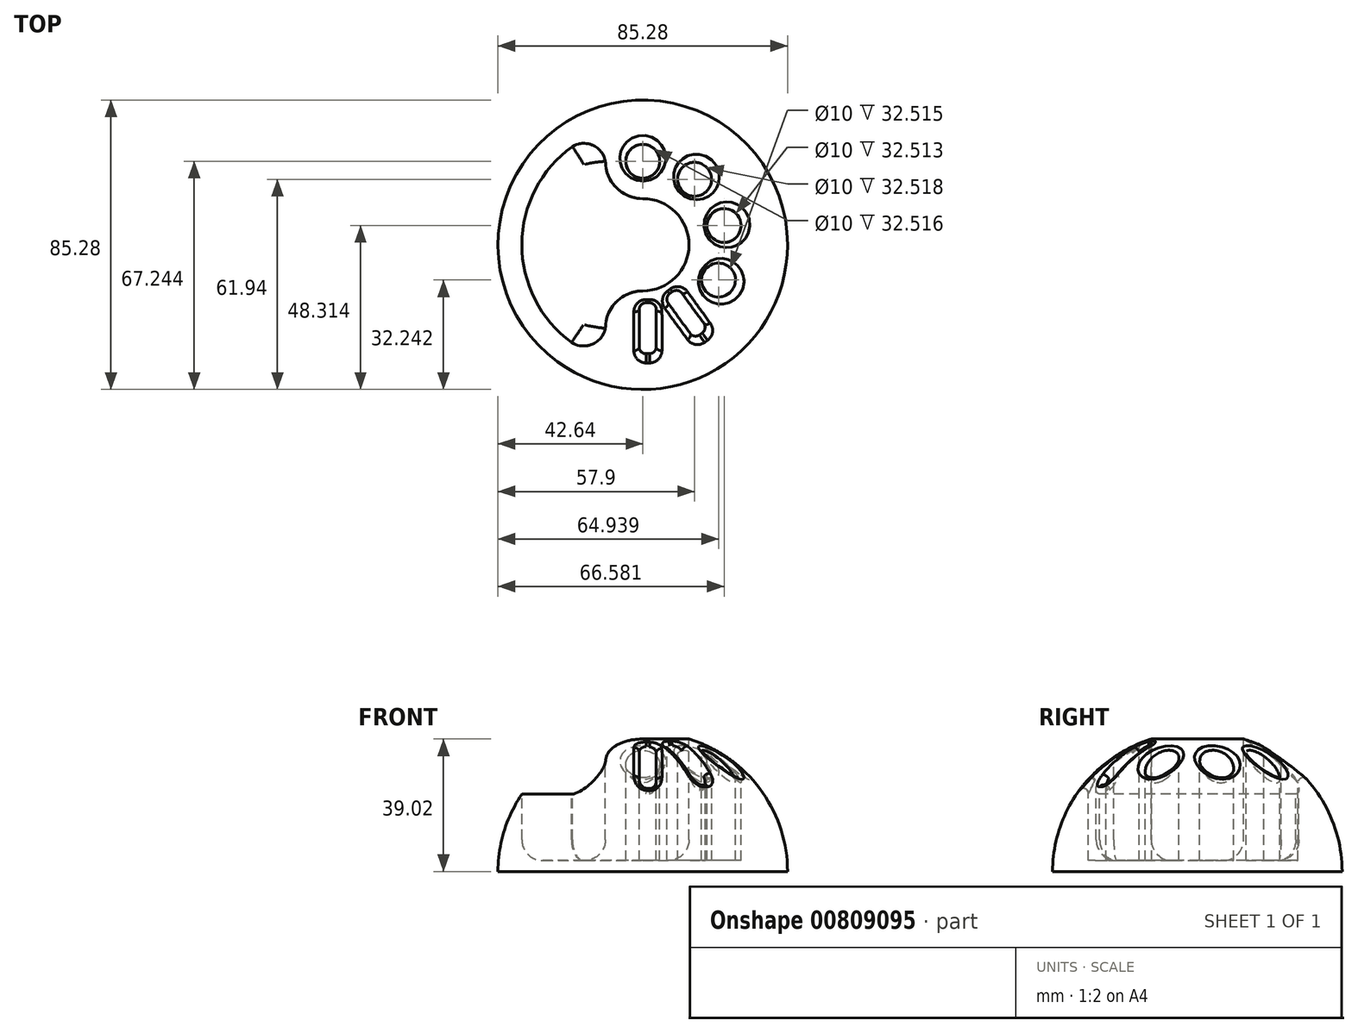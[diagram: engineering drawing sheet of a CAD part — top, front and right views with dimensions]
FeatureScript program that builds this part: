
annotation { "Feature Type Name" : "Feature", "Feature Type Description" : "" }
export const myFeature = defineFeature(function(context is Context, id is Id, definition is map)
    precondition{}
    {
        {
            var Q0;
            Q0=qCreatedBy(makeId("Top.planeOp"),FACE);
            var sketch = newSketch(context, id + "F0", { "sketchPlane" : qUnion([Q0])});
            skPoint(sketch, "E0.middle", {"position": v(0, 0) * mm});
            skCircle(sketch, "E1", {"center": v(0, 0) * mm, "radius": 42.64 * mm});
            skPoint(sketch, "E0.left.end.orphan", {"position": v(-44.45, 44.45) * mm});
            skPoint(sketch, "E0.bottom.start.orphan", {"position": v(-44.45, -44.45) * mm});
            skPoint(sketch, "E0.right.end.orphan", {"position": v(44.45, 44.45) * mm});
            skPoint(sketch, "E0.right.start.orphan", {"position": v(44.45, -44.45) * mm});
            skSolve(sketch);
        }
        {
            var Q0;
            Q0=makeQuery(id+"F0.imprint","IMPRINT",FACE,{"disambiguationData":[TD([[makeQuery(id+"F0.imprint","IMPRINT",EDGE,{"derivedFrom":sQuery(id+"F0.wireOp",EDGE,"E0.bottom")}),1.0]])]});
            var Q1;
            Q1=makeQuery(id+"F0.imprint","IMPRINT",FACE,{"disambiguationData":[TD([[makeQuery(id+"F0.imprint","IMPRINT",EDGE,{"derivedFrom":sQuery(id+"F0.wireOp",EDGE,"E1")}),1.0]])]});
            extrude(context, id + "F1", {"entities" : qUnion([Q0, Q1]), "depth" : 50.8 * mm, "offsetDistance" : 25.4 * mm, "hasSecondDirection" : true, "secondDirectionOppositeDirection" : false, "secondDirectionDepth" : 10 * mm});
        }
        {
            var Q0;
            Q0=makeQuery(id+"F1.opExtrude","CAP_FACE",FACE,{"disambiguationData":[OSD([sQuery(id+"F0.wireOp",EDGE,"E1")])],"isStart":false});
            var sketch = newSketch(context, id + "F2", { "sketchPlane" : qUnion([Q0])});
            skCircle(sketch, "E2", {"center": v(0, 24.6) * mm, "radius": 5 * mm});
            skCircle(sketch, "E3.1.0", {"center": v(15.26, 19.3) * mm, "radius": 5 * mm});
            skCircle(sketch, "E3.2.0", {"center": v(23.94, 5.67) * mm, "radius": 5 * mm});
            skCircle(sketch, "E3.3.0", {"center": v(22.3, -10.4) * mm, "radius": 5 * mm});
            skPoint(sketch, "E3.center", {"position": v(0, 0) * mm});
            skLineSegment(sketch, "E3.anchor1", {"start": v(0, 0) * mm, "end": v(0, 24.6) * mm, "construction": true});
            skLineSegment(sketch, "E3.anchor2", {"start": v(0, 0) * mm, "end": v(22.3, -10.4) * mm, "construction": true});
            skLineSegment(sketch, "E4.bottom", {"start": v(1.96, -32.1) * mm, "end": v(0.96, -32.1) * mm});
            skLineSegment(sketch, "E4.top", {"start": v(1.96, -17.1) * mm, "end": v(0.96, -17.1) * mm});
            skLineSegment(sketch, "E4.left", {"start": v(3.96, -30.1) * mm, "end": v(3.96, -19.1) * mm});
            skLineSegment(sketch, "E4.right", {"start": v(-1.04, -30.1) * mm, "end": v(-1.04, -19.1) * mm});
            skPoint(sketch, "E4.middle", {"position": v(1.46, -24.6) * mm});
            skPoint(sketch, "E5.visualSharp", {"position": v(-1.04, -17.1) * mm});
            skArc(sketch, "E5.filletArc", {"start": v(0.96, -17.1) * mm, "mid": v(-0.45, -17.68) * mm, "end": v(-1.04, -19.1) * mm});
            skPoint(sketch, "E6.visualSharp", {"position": v(3.96, -17.1) * mm});
            skArc(sketch, "E6.filletArc", {"start": v(3.96, -19.1) * mm, "mid": v(3.37, -17.68) * mm, "end": v(1.96, -17.1) * mm});
            skPoint(sketch, "E7.visualSharp", {"position": v(3.96, -32.1) * mm});
            skArc(sketch, "E7.filletArc", {"start": v(1.96, -32.1) * mm, "mid": v(3.37, -31.5) * mm, "end": v(3.96, -30.1) * mm});
            skPoint(sketch, "E8.visualSharp", {"position": v(-1.04, -32.1) * mm});
            skArc(sketch, "E8.filletArc", {"start": v(-1.04, -30.1) * mm, "mid": v(-0.45, -31.5) * mm, "end": v(0.96, -32.1) * mm});
            skPoint(sketch, "E9.1.0", {"position": v(10.33, -12.64) * mm});
            skLineSegment(sketch, "E9.1.1", {"start": v(17.98, -23.16) * mm, "end": v(11.5, -14.26) * mm});
            skArc(sketch, "E9.1.2", {"start": v(17.53, -25.95) * mm, "mid": v(18.33, -24.65) * mm, "end": v(17.98, -23.16) * mm});
            skArc(sketch, "E9.1.3", {"start": v(11.5, -14.26) * mm, "mid": v(10.2, -13.46) * mm, "end": v(8.72, -13.82) * mm});
            skLineSegment(sketch, "E9.1.4", {"start": v(8.72, -13.82) * mm, "end": v(7.9, -14.4) * mm});
            skArc(sketch, "E9.1.5", {"start": v(7.9, -14.4) * mm, "mid": v(7.1, -15.71) * mm, "end": v(7.46, -17.2) * mm});
            skLineSegment(sketch, "E9.1.6", {"start": v(13.93, -26.1) * mm, "end": v(7.46, -17.2) * mm});
            skArc(sketch, "E9.1.7", {"start": v(13.93, -26.1) * mm, "mid": v(15.24, -26.9) * mm, "end": v(16.72, -26.54) * mm});
            skLineSegment(sketch, "E9.1.8", {"start": v(17.53, -25.95) * mm, "end": v(16.72, -26.54) * mm});
            skPoint(sketch, "E9.center", {"position": v(0.3, -5.06) * mm});
            skLineSegment(sketch, "E9.anchor1", {"start": v(0.3, -5.06) * mm, "end": v(3.96, -19.1) * mm, "construction": true});
            skLineSegment(sketch, "E9.anchor2", {"start": v(0.3, -5.06) * mm, "end": v(11.5, -14.26) * mm, "construction": true});
            skArc(sketch, "E10", {"start": v(0, -13.6) * mm, "mid": v(13.6, 0) * mm, "end": v(0, 13.6) * mm});
            skArc(sketch, "E11", {"start": v(-11, 24.6) * mm, "mid": v(-7.78, 16.82) * mm, "end": v(0, 13.6) * mm});
            skArc(sketch, "E12", {"start": v(-20.72, 28.96) * mm, "mid": v(-35.6, 0.16) * mm, "end": v(-20.98, -28.77) * mm});
            skArc(sketch, "E13.1.0", {"start": v(0, -13.6) * mm, "mid": v(-7.78, -16.82) * mm, "end": v(-11, -24.6) * mm});
            skLineSegment(sketch, "E13.anchor2", {"start": v(0, 0) * mm, "end": v(0, -24.6) * mm, "construction": true});
            skArc(sketch, "E14", {"start": v(-11, 24.6) * mm, "mid": v(-15.28, 29.55) * mm, "end": v(-21.68, 28.25) * mm});
            skArc(sketch, "E15", {"start": v(-21.68, -28.25) * mm, "mid": v(-15.3, -29.48) * mm, "end": v(-11, -24.6) * mm});
            skSolve(sketch);
        }
        {
            var Q0;
            Q0=makeQuery(id+"F2.imprint","IMPRINT",FACE,{"disambiguationData":[TD([[makeQuery(id+"F2.imprint","IMPRINT",EDGE,{"derivedFrom":sQuery(id+"F2.wireOp",EDGE,"E10")}),1.0]])]});
            var Q1;
            Q1=makeQuery(id+"F2.imprint","IMPRINT",FACE,{"disambiguationData":[TD([[makeQuery(id+"F2.imprint","IMPRINT",EDGE,{"derivedFrom":sQuery(id+"F2.wireOp",EDGE,"E2")}),1.0]])]});
            var Q2;
            Q2=makeQuery(id+"F2.imprint","IMPRINT",FACE,{"disambiguationData":[TD([[makeQuery(id+"F2.imprint","IMPRINT",EDGE,{"derivedFrom":sQuery(id+"F2.wireOp",EDGE,"E3.1.0")}),1.0]])]});
            var Q3;
            Q3=makeQuery(id+"F2.imprint","IMPRINT",FACE,{"disambiguationData":[TD([[makeQuery(id+"F2.imprint","IMPRINT",EDGE,{"derivedFrom":sQuery(id+"F2.wireOp",EDGE,"E3.2.0")}),1.0]])]});
            var Q4;
            Q4=makeQuery(id+"F2.imprint","IMPRINT",FACE,{"disambiguationData":[TD([[makeQuery(id+"F2.imprint","IMPRINT",EDGE,{"derivedFrom":sQuery(id+"F2.wireOp",EDGE,"E3.3.0")}),1.0]])]});
            var Q5;
            Q5=makeQuery(id+"F2.imprint","IMPRINT",FACE,{"disambiguationData":[TD([[makeQuery(id+"F2.imprint","IMPRINT",EDGE,{"derivedFrom":sQuery(id+"F2.wireOp",EDGE,"E9.1.1")}),1.0]])]});
            var Q6;
            Q6=makeQuery(id+"F2.imprint","IMPRINT",FACE,{"disambiguationData":[TD([[makeQuery(id+"F2.imprint","IMPRINT",EDGE,{"derivedFrom":sQuery(id+"F2.wireOp",EDGE,"E4.bottom")}),-1.0]])]});
            extrude(context, id + "F3", {"entities" : qUnion([Q0, Q1, Q2, Q3, Q4, Q5, Q6]), "operationType" : NewBodyOperationType.REMOVE, "oppositeDirection" : true, "depth" : 37.6 * mm, "offsetDistance" : 25 * mm});
        }
        {
            var Q0;
            Q0=makeQuery(id+"F1.opExtrude","CAP_EDGE",EDGE,{"disambiguationData":[OSD([sQuery(id+"F0.wireOp",EDGE,"E1")])],"isStart":false});
            fillet(context, id + "F4", {"entities" : qUnion([Q0]), "radius" : 40.97 * mm, "tangentPropagation" : true, "allowEdgeOverflow" : false});
        }
        {
            var Q0;
            Q0=makeQuery(id+"F3.boolean.opBoolean","COPY",FACE,{"derivedFrom":makeQuery(id+"F3.opExtrude","CAP_FACE",FACE,{"disambiguationData":[OSD([sQuery(id+"F2.wireOp",EDGE,"E10"),sQuery(id+"F2.wireOp",EDGE,"E11"),sQuery(id+"F2.wireOp",EDGE,"E12"),sQuery(id+"F2.wireOp",EDGE,"E13.1.0"),sQuery(id+"F2.wireOp",EDGE,"E14"),sQuery(id+"F2.wireOp",EDGE,"E15")])],"isStart":false})});
            fillet(context, id + "F5", {"entities" : qUnion([Q0]), "radius" : 6.16 * mm, "tangentPropagation" : true, "allowEdgeOverflow" : false});
        }
        {
            var Q0;
            Q0=makeQuery(id+"F4.opFillet","BLEND_EDGE",EDGE,{"blendedFrom":[makeQuery(id+"F1.opExtrude","CAP_EDGE",EDGE,{"disambiguationData":[OSD([sQuery(id+"F0.wireOp",EDGE,"E1")])],"isStart":false}),makeQuery(id+"F3.boolean.opBoolean","COPY",FACE,{"derivedFrom":makeQuery(id+"F3.opExtrude","SWEPT_FACE",FACE,{"disambiguationData":[OSD([sQuery(id+"F2.wireOp",EDGE,"E2")])]})})],"blendedInto":[makeQuery(id+"F3.boolean.opBoolean","COPY",FACE,{"derivedFrom":makeQuery(id+"F3.opExtrude","SWEPT_FACE",FACE,{"disambiguationData":[OSD([sQuery(id+"F2.wireOp",EDGE,"E2")])]})})]});
            var Q1;
            Q1=makeQuery(id+"F4.opFillet","BLEND_EDGE",EDGE,{"blendedFrom":[makeQuery(id+"F1.opExtrude","CAP_EDGE",EDGE,{"disambiguationData":[OSD([sQuery(id+"F0.wireOp",EDGE,"E1")])],"isStart":false}),makeQuery(id+"F3.boolean.opBoolean","COPY",FACE,{"derivedFrom":makeQuery(id+"F3.opExtrude","SWEPT_FACE",FACE,{"disambiguationData":[OSD([sQuery(id+"F2.wireOp",EDGE,"E3.1.0")])]})})],"blendedInto":[makeQuery(id+"F3.boolean.opBoolean","COPY",FACE,{"derivedFrom":makeQuery(id+"F3.opExtrude","SWEPT_FACE",FACE,{"disambiguationData":[OSD([sQuery(id+"F2.wireOp",EDGE,"E3.1.0")])]})})]});
            var Q2;
            Q2=makeQuery(id+"F4.opFillet","BLEND_EDGE",EDGE,{"blendedFrom":[makeQuery(id+"F1.opExtrude","CAP_EDGE",EDGE,{"disambiguationData":[OSD([sQuery(id+"F0.wireOp",EDGE,"E1")])],"isStart":false}),makeQuery(id+"F3.boolean.opBoolean","COPY",FACE,{"derivedFrom":makeQuery(id+"F3.opExtrude","SWEPT_FACE",FACE,{"disambiguationData":[OSD([sQuery(id+"F2.wireOp",EDGE,"E3.2.0")])]})})],"blendedInto":[makeQuery(id+"F3.boolean.opBoolean","COPY",FACE,{"derivedFrom":makeQuery(id+"F3.opExtrude","SWEPT_FACE",FACE,{"disambiguationData":[OSD([sQuery(id+"F2.wireOp",EDGE,"E3.2.0")])]})})]});
            var Q3;
            Q3=makeQuery(id+"F4.opFillet","BLEND_EDGE",EDGE,{"blendedFrom":[makeQuery(id+"F1.opExtrude","CAP_EDGE",EDGE,{"disambiguationData":[OSD([sQuery(id+"F0.wireOp",EDGE,"E1")])],"isStart":false}),makeQuery(id+"F3.boolean.opBoolean","COPY",FACE,{"derivedFrom":makeQuery(id+"F3.opExtrude","SWEPT_FACE",FACE,{"disambiguationData":[OSD([sQuery(id+"F2.wireOp",EDGE,"E3.3.0")])]})})],"blendedInto":[makeQuery(id+"F3.boolean.opBoolean","COPY",FACE,{"derivedFrom":makeQuery(id+"F3.opExtrude","SWEPT_FACE",FACE,{"disambiguationData":[OSD([sQuery(id+"F2.wireOp",EDGE,"E3.3.0")])]})})]});
            var Q4;
            Q4=makeQuery(id+"F4.opFillet","BLEND_EDGE",EDGE,{"blendedFrom":[makeQuery(id+"F1.opExtrude","CAP_EDGE",EDGE,{"disambiguationData":[OSD([sQuery(id+"F0.wireOp",EDGE,"E1")])],"isStart":false}),makeQuery(id+"F3.boolean.opBoolean","COPY",FACE,{"derivedFrom":makeQuery(id+"F3.opExtrude","SWEPT_FACE",FACE,{"disambiguationData":[OSD([sQuery(id+"F2.wireOp",EDGE,"E4.left")])]})})],"blendedInto":[makeQuery(id+"F3.boolean.opBoolean","COPY",FACE,{"derivedFrom":makeQuery(id+"F3.opExtrude","SWEPT_FACE",FACE,{"disambiguationData":[OSD([sQuery(id+"F2.wireOp",EDGE,"E4.left")])]})})]});
            var Q5;
            Q5=makeQuery(id+"F4.opFillet","BLEND_EDGE",EDGE,{"blendedFrom":[makeQuery(id+"F1.opExtrude","CAP_EDGE",EDGE,{"disambiguationData":[OSD([sQuery(id+"F0.wireOp",EDGE,"E1")])],"isStart":false}),makeQuery(id+"F3.boolean.opBoolean","COPY",FACE,{"derivedFrom":makeQuery(id+"F3.opExtrude","SWEPT_FACE",FACE,{"disambiguationData":[OSD([sQuery(id+"F2.wireOp",EDGE,"E9.1.6")])]})})],"blendedInto":[makeQuery(id+"F3.boolean.opBoolean","COPY",FACE,{"derivedFrom":makeQuery(id+"F3.opExtrude","SWEPT_FACE",FACE,{"disambiguationData":[OSD([sQuery(id+"F2.wireOp",EDGE,"E9.1.6")])]})})]});
            var Q6;
            Q6=makeQuery(id+"F4.opFillet","BLEND_EDGE",EDGE,{"blendedFrom":[makeQuery(id+"F1.opExtrude","CAP_EDGE",EDGE,{"disambiguationData":[OSD([sQuery(id+"F0.wireOp",EDGE,"E1")])],"isStart":false}),makeQuery(id+"F3.boolean.opBoolean","COPY",FACE,{"derivedFrom":makeQuery(id+"F3.opExtrude","SWEPT_FACE",FACE,{"disambiguationData":[OSD([sQuery(id+"F2.wireOp",EDGE,"E9.1.7")])]})})],"blendedInto":[makeQuery(id+"F3.boolean.opBoolean","COPY",FACE,{"derivedFrom":makeQuery(id+"F3.opExtrude","SWEPT_FACE",FACE,{"disambiguationData":[OSD([sQuery(id+"F2.wireOp",EDGE,"E9.1.7")])]})})]});
            fillet(context, id + "F6", {"entities" : qUnion([Q0, Q1, Q2, Q3, Q4, Q5, Q6]), "radius" : 1.5 * mm, "tangentPropagation" : true, "allowEdgeOverflow" : false});
        }
    });
